# Revit family: Fireplace_Gas_Heatilator_Crave-See-Thru
name_source: partatom
category: Mechanical Equipment
revit_build: Autodesk Revit 2015 (Build: 20140323_1530(x64)
units: mm (PartAtom-declared; Revit-internal decimal feet)

## types (4) — shared parameters
Assembly Code = D3020
Construction Details = http://www.arcat.com
Default Elevation = 0' - 0"
Electrical_Voltage = 120 V
Fixture Finish = Metal - Heatilator - Metallic Black
Fuel Consumption = as Specified
HVAC_BTU Output = 0.0 Btu/h
Heating Capacity = as Specified
Keynote = 10305
Manufacturer = Heatilator
Manufacturer Website = http://www.heatilator.com
Opening Height = 1' - 3 5/8"
Product Data = http://www.arcat.com
Revision = R2_2014-09
Sales Information = http://www.heatilator.com
Send Message = http://www.arcat.com
Specification = http://www.arcat.com
Standards Conformance = UL  ;  cUL
URL = http://www.heatilator.com
Unit Depth = 1' - 6 1/8"
Unit Height = 3' - 6 1/2"
zero-valued in all types: Expected Lifespan (Years), Maintenance Schedule (Months), Warranty Duration (Years)

## per-type parameters (varying)
| type | Description | Efficiency Ratings | Fuel Type | HVAC_BTU Input | Model | Opening Width | Unit Weight | Unit Width |
| 48x13 Viewing Area LP | Heatilator Gas Burning Fireplace - Crave See-Thru CRAVE6048ST LP as Specified | Steady State 58.3  ;  AFUE 48.3  ;  EnerGuide 51.3 | LP | 36000.0 Btu/h | CRAVE6048ST | 4' - 3 1/8" | 250 | 5' - 2" |
| 48x13 Viewing Area NG | Heatilator Gas Burning Fireplace - Crave See-Thru CRAVE6048ST NG as Specified | Steady State 58.3  ;  AFUE 48.3  ;  EnerGuide 51.3 | NG | 40000.0 Btu/h | CRAVE6048ST | 4' - 3 1/8" | 250 | 5' - 2" |
| 36x13 Viewing Area LP | Heatilator Gas Burning Fireplace - Crave See-Thru CRAVE4836ST LP as Specified | Steady State 49.3  ;  AFUE 39.7  ;  EnerGuide 45.9 | LP | 29000.0 Btu/h | CRAVE4836ST | 3' - 3 1/4" | 200 | 4' - 2" |
| 36x13 Viewing Area NG | Heatilator Gas Burning Fireplace - Crave See-Thru CRAVE4836ST NG as Specified | Steady State 49.3  ;  AFUE 39.7  ;  EnerGuide 45.9 | NG | 30000.0 Btu/h | CRAVE4836ST | 3' - 3 1/4" | 200 | 4' - 2" |

## geometry (parser evidence)
native form markers: Blend x6, Sweep x4
no freeform markers — native parametric forms only
